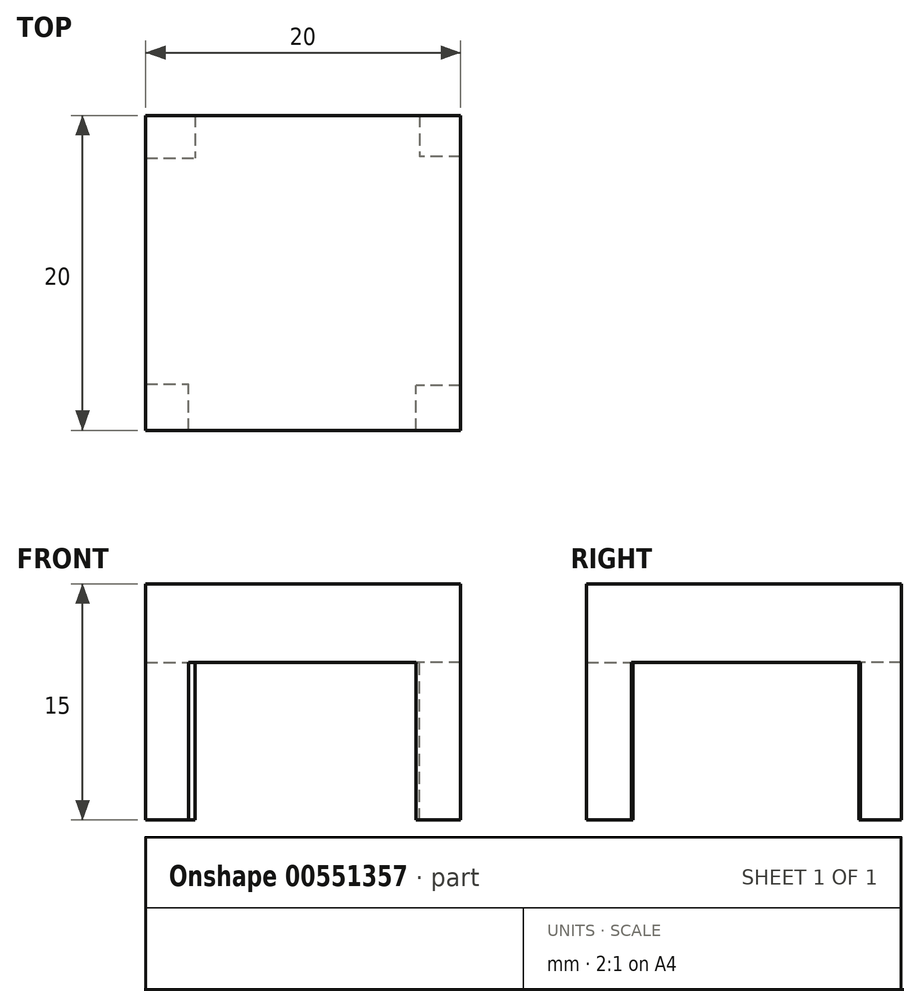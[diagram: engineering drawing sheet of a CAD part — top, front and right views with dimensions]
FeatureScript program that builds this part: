
annotation { "Feature Type Name" : "Feature", "Feature Type Description" : "" }
export const myFeature = defineFeature(function(context is Context, id is Id, definition is map)
    precondition{}
    {
        {
            var Q0;
            Q0=qCreatedBy(makeId("Top.planeOp"),FACE);
            var sketch = newSketch(context, id + "F0", { "sketchPlane" : qUnion([Q0])});
            skLineSegment(sketch, "E0.bottom", {"start": v(-10, 10) * mm, "end": v(10, 10) * mm});
            skLineSegment(sketch, "E0.top", {"start": v(-10, -10) * mm, "end": v(10, -10) * mm});
            skLineSegment(sketch, "E0.left", {"start": v(-10, 10) * mm, "end": v(-10, -10) * mm});
            skLineSegment(sketch, "E0.right", {"start": v(10, 10) * mm, "end": v(10, -10) * mm});
            skPoint(sketch, "E0.middle", {"position": v(0, 0) * mm});
            skSolve(sketch);
        }
        {
            var Q0;
            Q0 = qSketchRegion(id + "F0", true);
            extrude(context, id + "F1", {"entities" : qUnion([Q0]), "depth" : 5 * mm, "offsetDistance" : 25 * mm});
        }
        {
            var Q0;
            Q0=makeQuery(id+"F1.opExtrude","CAP_FACE",FACE,{"disambiguationData":[OSD([sQuery(id+"F0.wireOp",EDGE,"E0.bottom"),sQuery(id+"F0.wireOp",EDGE,"E0.top"),sQuery(id+"F0.wireOp",EDGE,"E0.left"),sQuery(id+"F0.wireOp",EDGE,"E0.right")])],"isStart":true});
            var sketch = newSketch(context, id + "F2", { "sketchPlane" : qUnion([Q0])});
            skLineSegment(sketch, "E1.bottom", {"start": v(-10, 10) * mm, "end": v(-7.28, 10) * mm});
            skLineSegment(sketch, "E1.top", {"start": v(-10, 7.05) * mm, "end": v(-7.28, 7.05) * mm});
            skLineSegment(sketch, "E1.left", {"start": v(-10, 10) * mm, "end": v(-10, 7.05) * mm});
            skLineSegment(sketch, "E1.right", {"start": v(-7.28, 10) * mm, "end": v(-7.28, 7.05) * mm});
            skLineSegment(sketch, "E2.bottom", {"start": v(10, 10) * mm, "end": v(7.17, 10) * mm});
            skLineSegment(sketch, "E2.top", {"start": v(10, 7.16) * mm, "end": v(7.17, 7.16) * mm});
            skLineSegment(sketch, "E2.left", {"start": v(10, 10) * mm, "end": v(10, 7.16) * mm});
            skLineSegment(sketch, "E2.right", {"start": v(7.17, 10) * mm, "end": v(7.17, 7.16) * mm});
            skLineSegment(sketch, "E3.bottom", {"start": v(10, -10) * mm, "end": v(7.38, -10) * mm});
            skLineSegment(sketch, "E3.top", {"start": v(10, -7.4) * mm, "end": v(7.38, -7.4) * mm});
            skLineSegment(sketch, "E3.left", {"start": v(10, -10) * mm, "end": v(10, -7.4) * mm});
            skLineSegment(sketch, "E3.right", {"start": v(7.38, -10) * mm, "end": v(7.38, -7.4) * mm});
            skLineSegment(sketch, "E4.bottom", {"start": v(-10, -10) * mm, "end": v(-6.86, -10) * mm});
            skLineSegment(sketch, "E4.top", {"start": v(-10, -7.29) * mm, "end": v(-6.86, -7.29) * mm});
            skLineSegment(sketch, "E4.left", {"start": v(-10, -10) * mm, "end": v(-10, -7.29) * mm});
            skLineSegment(sketch, "E4.right", {"start": v(-6.86, -10) * mm, "end": v(-6.86, -7.29) * mm});
            skSolve(sketch);
        }
        {
            var Q0;
            Q0 = qSketchRegion(id + "F2", true);
            extrude(context, id + "F3", {"entities" : qUnion([Q0]), "operationType" : NewBodyOperationType.ADD, "depth" : 10 * mm, "offsetDistance" : 25 * mm});
        }
    });
